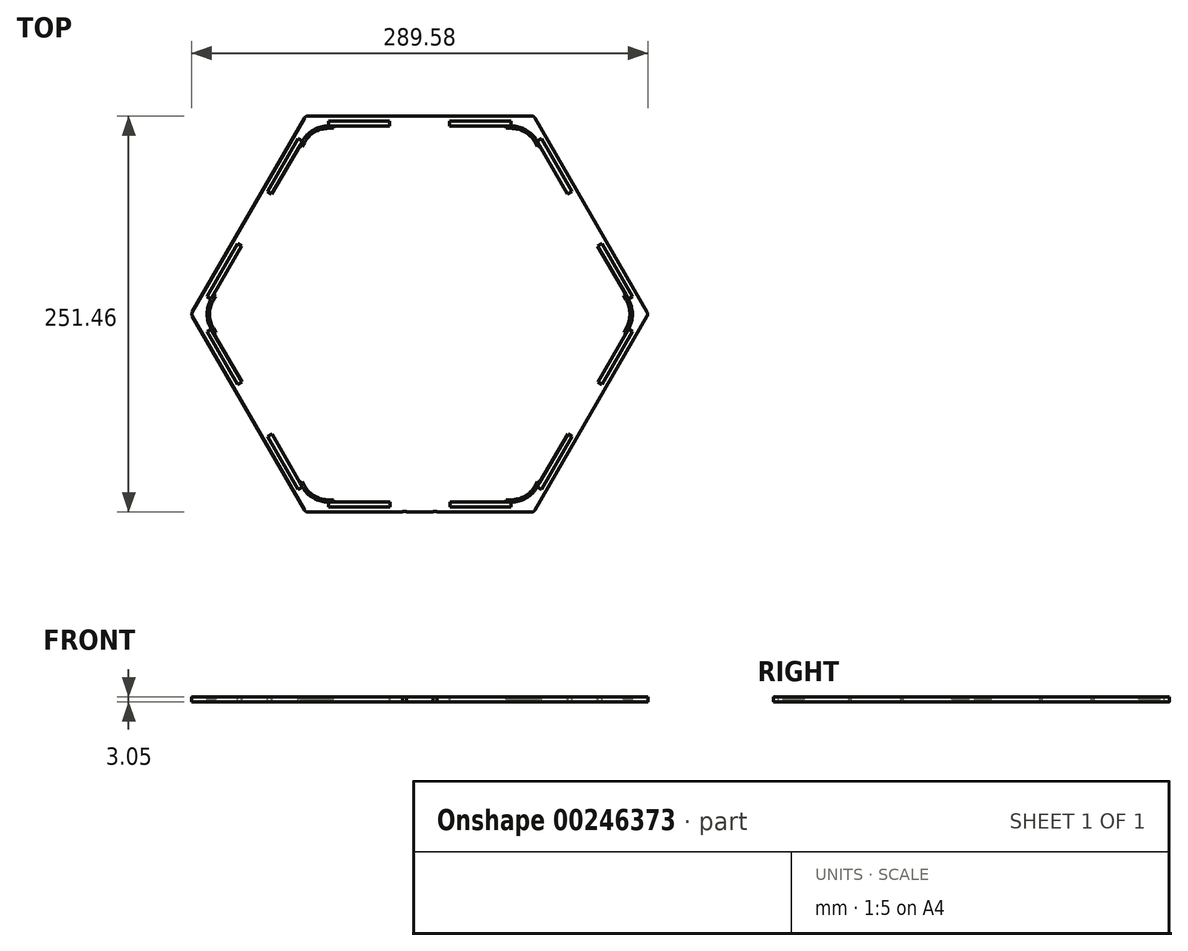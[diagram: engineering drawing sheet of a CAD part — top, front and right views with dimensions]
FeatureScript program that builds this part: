
annotation { "Feature Type Name" : "Feature", "Feature Type Description" : "" }
export const myFeature = defineFeature(function(context is Context, id is Id, definition is map)
    precondition{}
    {
        {
            var Q0;
            Q0=qCreatedBy(makeId("Top.planeOp"),FACE);
            var sketch = newSketch(context, id + "F0", { "sketchPlane" : qUnion([Q0])});
            skCircle(sketch, "E0.cCircle", {"center": v(0, 0) * mm, "radius": 125.73 * mm, "construction": true});
            skLineSegment(sketch, "E0.0", {"start": v(-137.85, 12.7) * mm, "end": v(-79.92, 113.03) * mm});
            skLineSegment(sketch, "E0.1", {"start": v(-57.93, 125.73) * mm, "end": v(57.93, 125.73) * mm});
            skLineSegment(sketch, "E0.2", {"start": v(79.92, 113.03) * mm, "end": v(137.85, 12.7) * mm});
            skLineSegment(sketch, "E0.3", {"start": v(137.85, -12.7) * mm, "end": v(79.92, -113.03) * mm});
            skLineSegment(sketch, "E0.4", {"start": v(57.93, -125.73) * mm, "end": v(-57.93, -125.73) * mm});
            skLineSegment(sketch, "E0.5", {"start": v(-79.92, -113.03) * mm, "end": v(-137.85, -12.7) * mm});
            skPoint(sketch, "E0.0.midPoint", {"position": v(-108.89, 62.87) * mm});
            skPoint(sketch, "E1.visualSharp", {"position": v(-72.6, 125.73) * mm});
            skArc(sketch, "E1.filletArc", {"start": v(-57.93, 125.73) * mm, "mid": v(-70.63, 122.33) * mm, "end": v(-79.92, 113.03) * mm});
            skPoint(sketch, "E2.visualSharp", {"position": v(72.6, 125.73) * mm});
            skArc(sketch, "E2.filletArc", {"start": v(79.92, 113.03) * mm, "mid": v(70.63, 122.33) * mm, "end": v(57.93, 125.73) * mm});
            skPoint(sketch, "E3.visualSharp", {"position": v(145.18, 0) * mm});
            skArc(sketch, "E3.filletArc", {"start": v(137.85, -12.7) * mm, "mid": v(141.25, 0) * mm, "end": v(137.85, 12.7) * mm});
            skPoint(sketch, "E4.visualSharp", {"position": v(72.6, -125.73) * mm});
            skArc(sketch, "E4.filletArc", {"start": v(57.93, -125.73) * mm, "mid": v(70.63, -122.33) * mm, "end": v(79.92, -113.03) * mm});
            skPoint(sketch, "E5.visualSharp", {"position": v(-72.6, -125.73) * mm});
            skArc(sketch, "E5.filletArc", {"start": v(-79.92, -113.03) * mm, "mid": v(-70.63, -122.33) * mm, "end": v(-57.93, -125.73) * mm});
            skPoint(sketch, "E6.visualSharp", {"position": v(-145.18, 0) * mm});
            skArc(sketch, "E6.filletArc", {"start": v(-137.85, 12.7) * mm, "mid": v(-141.25, 0) * mm, "end": v(-137.85, -12.7) * mm});
            skSolve(sketch);
        }
        {
            var Q0;
            Q0=qSketchRegion(id+"F0",true);
            extrude(context, id + "F1", {"entities" : qUnion([Q0]), "depth" : 3.05 * mm});
        }
        {
            var Q0;
            Q0=makeQuery(id+"F1.opExtrude","CAP_FACE",FACE,{"disambiguationData":[OSD([sQuery(id+"F0.wireOp",EDGE,"E0.0"),sQuery(id+"F0.wireOp",EDGE,"E0.1"),sQuery(id+"F0.wireOp",EDGE,"E0.2"),sQuery(id+"F0.wireOp",EDGE,"E0.3"),sQuery(id+"F0.wireOp",EDGE,"E0.4"),sQuery(id+"F0.wireOp",EDGE,"E0.5"),sQuery(id+"F0.wireOp",EDGE,"E1.filletArc"),sQuery(id+"F0.wireOp",EDGE,"E2.filletArc"),sQuery(id+"F0.wireOp",EDGE,"E3.filletArc"),sQuery(id+"F0.wireOp",EDGE,"E4.filletArc"),sQuery(id+"F0.wireOp",EDGE,"E5.filletArc"),sQuery(id+"F0.wireOp",EDGE,"E6.filletArc")])],"isStart":false});
            var sketch = newSketch(context, id + "F2", { "sketchPlane" : qUnion([Q0])});
            skLineSegment(sketch, "E7", {"start": v(-57.93, 122.56) * mm, "end": v(-57.93, 119.5) * mm});
            skLineSegment(sketch, "E8", {"start": v(-57.93, 119.5) * mm, "end": v(57.8, 119.5) * mm});
            skLineSegment(sketch, "E9", {"start": v(57.8, 119.5) * mm, "end": v(57.8, 122.56) * mm});
            skLineSegment(sketch, "E10.1.0", {"start": v(-135.1, 11.11) * mm, "end": v(-132.46, 9.59) * mm});
            skLineSegment(sketch, "E10.1.1", {"start": v(-132.46, 9.59) * mm, "end": v(-74.6, 109.82) * mm});
            skLineSegment(sketch, "E10.1.2", {"start": v(-74.6, 109.82) * mm, "end": v(-77.23, 111.34) * mm});
            skLineSegment(sketch, "E10.2.0", {"start": v(-77.17, -111.44) * mm, "end": v(-74.53, -109.92) * mm});
            skLineSegment(sketch, "E10.2.1", {"start": v(-74.53, -109.92) * mm, "end": v(-132.4, -9.7) * mm});
            skLineSegment(sketch, "E10.2.2", {"start": v(-132.4, -9.7) * mm, "end": v(-135.04, -11.22) * mm});
            skLineSegment(sketch, "E10.3.0", {"start": v(57.93, -122.55) * mm, "end": v(57.93, -119.5) * mm});
            skLineSegment(sketch, "E10.3.1", {"start": v(57.93, -119.5) * mm, "end": v(-57.8, -119.5) * mm});
            skLineSegment(sketch, "E10.3.2", {"start": v(-57.8, -119.5) * mm, "end": v(-57.8, -122.55) * mm});
            skLineSegment(sketch, "E10.4.0", {"start": v(135.1, -11.11) * mm, "end": v(132.46, -9.59) * mm});
            skLineSegment(sketch, "E10.4.1", {"start": v(132.46, -9.59) * mm, "end": v(74.6, -109.82) * mm});
            skLineSegment(sketch, "E10.4.2", {"start": v(74.6, -109.82) * mm, "end": v(77.23, -111.34) * mm});
            skLineSegment(sketch, "E10.5.0", {"start": v(77.17, 111.44) * mm, "end": v(74.53, 109.92) * mm});
            skLineSegment(sketch, "E10.5.1", {"start": v(74.53, 109.92) * mm, "end": v(132.4, 9.7) * mm});
            skLineSegment(sketch, "E10.5.2", {"start": v(132.4, 9.7) * mm, "end": v(135.04, 11.22) * mm});
            skPoint(sketch, "E10.center", {"position": v(0, 0) * mm});
            skLineSegment(sketch, "E11", {"start": v(-57.93, 122.56) * mm, "end": v(57.8, 122.56) * mm});
            skLineSegment(sketch, "E12.1.0", {"start": v(-135.1, 11.11) * mm, "end": v(-77.23, 111.34) * mm});
            skLineSegment(sketch, "E12.2.0", {"start": v(-77.17, -111.44) * mm, "end": v(-135.04, -11.22) * mm});
            skLineSegment(sketch, "E12.3.0", {"start": v(57.93, -122.56) * mm, "end": v(-57.8, -122.56) * mm});
            skLineSegment(sketch, "E12.4.0", {"start": v(135.1, -11.11) * mm, "end": v(77.23, -111.34) * mm});
            skLineSegment(sketch, "E12.5.0", {"start": v(77.17, 111.44) * mm, "end": v(135.04, 11.22) * mm});
            skSolve(sketch);
        }
        {
            var Q0;
            Q0=makeQuery(id+"F2.imprint","IMPRINT",FACE,{"disambiguationData":[TD([[makeQuery(id+"F2.imprint","IMPRINT",EDGE,{"derivedFrom":sQuery(id+"F2.wireOp",EDGE,"E10.2.0")}),1.0]])]});
            var Q1;
            Q1=makeQuery(id+"F2.imprint","IMPRINT",FACE,{"disambiguationData":[TD([[makeQuery(id+"F2.imprint","IMPRINT",EDGE,{"derivedFrom":sQuery(id+"F2.wireOp",EDGE,"E10.1.0")}),1.0]])]});
            var Q2;
            Q2=makeQuery(id+"F2.imprint","IMPRINT",FACE,{"disambiguationData":[TD([[makeQuery(id+"F2.imprint","IMPRINT",EDGE,{"derivedFrom":sQuery(id+"F2.wireOp",EDGE,"E7")}),1.0]])]});
            var Q3;
            Q3=makeQuery(id+"F2.imprint","IMPRINT",FACE,{"disambiguationData":[TD([[makeQuery(id+"F2.imprint","IMPRINT",EDGE,{"derivedFrom":sQuery(id+"F2.wireOp",EDGE,"E10.5.0")}),1.0]])]});
            var Q4;
            Q4=makeQuery(id+"F2.imprint","IMPRINT",FACE,{"disambiguationData":[TD([[makeQuery(id+"F2.imprint","IMPRINT",EDGE,{"derivedFrom":sQuery(id+"F2.wireOp",EDGE,"E10.4.0")}),1.0]])]});
            var Q5;
            Q5=makeQuery(id+"F2.imprint","IMPRINT",FACE,{"disambiguationData":[TD([[makeQuery(id+"F2.imprint","IMPRINT",EDGE,{"derivedFrom":sQuery(id+"F2.wireOp",EDGE,"E10.3.0")}),1.0]])]});
            extrude(context, id + "F3", {"entities" : qUnion([Q0, Q1, Q2, Q3, Q4, Q5]), "operationType" : NewBodyOperationType.REMOVE, "endBound" : BoundingType.THROUGH_ALL, "oppositeDirection" : true, "depth" : 25.4 * mm});
        }
        {
            var Q0;
            Q0=makeQuery(id+"F2.imprint","IMPRINT",FACE,{"disambiguationData":[TD([[makeQuery(id+"F2.imprint","IMPRINT",EDGE,{"derivedFrom":sQuery(id+"F2.wireOp",EDGE,"E7")}),-1.0]])]});
            var sketch = newSketch(context, id + "F4", { "sketchPlane" : qUnion([Q0])});
            skCircle(sketch, "E13", {"center": v(-62.3, 107.85) * mm, "radius": 7.89 * mm});
            skArc(sketch, "E14", {"start": v(-57.93, 119.5) * mm, "mid": v(-67.57, 116.9) * mm, "end": v(-74.6, 109.82) * mm, "construction": true});
            skLineSegment(sketch, "E15", {"start": v(-67.57, 116.9) * mm, "end": v(-62.3, 107.85) * mm, "construction": true});
            skPoint(sketch, "E16", {"position": v(-66.26, 114.67) * mm});
            skCircle(sketch, "E17.1.0", {"center": v(-124.55, -0.03) * mm, "radius": 7.89 * mm});
            skCircle(sketch, "E17.2.0", {"center": v(-62.25, -107.88) * mm, "radius": 7.89 * mm});
            skCircle(sketch, "E17.3.0", {"center": v(62.3, -107.85) * mm, "radius": 7.89 * mm});
            skCircle(sketch, "E17.4.0", {"center": v(124.55, 0.03) * mm, "radius": 7.89 * mm});
            skCircle(sketch, "E17.5.0", {"center": v(62.25, 107.88) * mm, "radius": 7.89 * mm});
            skPoint(sketch, "E17.center", {"position": v(0, 0) * mm});
            skSolve(sketch);
        }
        {
            var Q0;
            Q0=makeQuery(id+"F1.opExtrude","CAP_FACE",FACE,{"disambiguationData":[OSD([sQuery(id+"F0.wireOp",EDGE,"E0.0"),sQuery(id+"F0.wireOp",EDGE,"E0.1"),sQuery(id+"F0.wireOp",EDGE,"E0.2"),sQuery(id+"F0.wireOp",EDGE,"E0.3"),sQuery(id+"F0.wireOp",EDGE,"E0.4"),sQuery(id+"F0.wireOp",EDGE,"E0.5"),sQuery(id+"F0.wireOp",EDGE,"E1.filletArc"),sQuery(id+"F0.wireOp",EDGE,"E2.filletArc"),sQuery(id+"F0.wireOp",EDGE,"E3.filletArc"),sQuery(id+"F0.wireOp",EDGE,"E4.filletArc"),sQuery(id+"F0.wireOp",EDGE,"E5.filletArc"),sQuery(id+"F0.wireOp",EDGE,"E6.filletArc")])],"isStart":false});
            var sketch = newSketch(context, id + "F5", { "sketchPlane" : qUnion([Q0])});
            skPoint(sketch, "E18", {"position": v(0, -122.56) * mm});
            skPoint(sketch, "E19", {"position": v(9.58, -122.56) * mm});
            skPoint(sketch, "E20", {"position": v(-9.53, -122.56) * mm});
            skLineSegment(sketch, "E21.bottom", {"start": v(-10.8, -125.73) * mm, "end": v(-8.26, -125.73) * mm});
            skLineSegment(sketch, "E21.top", {"start": v(-10.8, -125.48) * mm, "end": v(-8.25, -125.48) * mm});
            skLineSegment(sketch, "E21.left", {"start": v(-10.8, -125.73) * mm, "end": v(-10.8, -125.48) * mm});
            skLineSegment(sketch, "E21.right", {"start": v(-8.25, -125.73) * mm, "end": v(-8.25, -125.48) * mm});
            skLineSegment(sketch, "E22.bottom", {"start": v(8.31, -125.73) * mm, "end": v(10.85, -125.73) * mm});
            skLineSegment(sketch, "E22.top", {"start": v(8.31, -125.48) * mm, "end": v(10.85, -125.48) * mm});
            skLineSegment(sketch, "E22.left", {"start": v(8.31, -125.73) * mm, "end": v(8.31, -125.48) * mm});
            skLineSegment(sketch, "E22.right", {"start": v(10.85, -125.73) * mm, "end": v(10.85, -125.48) * mm});
            skPoint(sketch, "E23", {"position": v(-9.53, -125.48) * mm});
            skPoint(sketch, "E24", {"position": v(9.58, -125.48) * mm});
            skSolve(sketch);
        }
        {
            var Q0;
            Q0=qSketchRegion(id+"F5",true);
            extrude(context, id + "F6", {"entities" : qUnion([Q0]), "operationType" : NewBodyOperationType.REMOVE, "endBound" : BoundingType.THROUGH_ALL, "oppositeDirection" : true, "depth" : 25.4 * mm});
        }
        {
            var Q0;
            Q0=makeQuery(id+"F1.opExtrude","CAP_FACE",FACE,{"disambiguationData":[OSD([sQuery(id+"F0.wireOp",EDGE,"E0.0"),sQuery(id+"F0.wireOp",EDGE,"E0.1"),sQuery(id+"F0.wireOp",EDGE,"E0.2"),sQuery(id+"F0.wireOp",EDGE,"E0.3"),sQuery(id+"F0.wireOp",EDGE,"E0.4"),sQuery(id+"F0.wireOp",EDGE,"E0.5"),sQuery(id+"F0.wireOp",EDGE,"E1.filletArc"),sQuery(id+"F0.wireOp",EDGE,"E2.filletArc"),sQuery(id+"F0.wireOp",EDGE,"E3.filletArc"),sQuery(id+"F0.wireOp",EDGE,"E4.filletArc"),sQuery(id+"F0.wireOp",EDGE,"E5.filletArc"),sQuery(id+"F0.wireOp",EDGE,"E6.filletArc")])],"isStart":false});
            var sketch = newSketch(context, id + "F7", { "sketchPlane" : qUnion([Q0])});
            skLineSegment(sketch, "E25", {"start": v(-79.92, 113.03) * mm, "end": v(-73.32, 124.46) * mm});
            skLineSegment(sketch, "E26", {"start": v(-71.12, 125.73) * mm, "end": v(-57.93, 125.73) * mm});
            skPoint(sketch, "E27.visualSharp", {"position": v(-72.6, 125.73) * mm});
            skArc(sketch, "E27.filletArc", {"start": v(-71.12, 125.73) * mm, "mid": v(-72.4, 125.39) * mm, "end": v(-73.32, 124.46) * mm});
            skLineSegment(sketch, "E28", {"start": v(-79.92, 113.03) * mm, "end": v(-57.93, 125.73) * mm});
            skLineSegment(sketch, "E29", {"start": v(57.93, 125.73) * mm, "end": v(71.12, 125.73) * mm});
            skLineSegment(sketch, "E30", {"start": v(73.32, 124.46) * mm, "end": v(79.92, 113.03) * mm});
            skLineSegment(sketch, "E31", {"start": v(-137.85, -12.7) * mm, "end": v(-144.45, -1.27) * mm});
            skLineSegment(sketch, "E32", {"start": v(-144.45, 1.27) * mm, "end": v(-137.85, 12.7) * mm});
            skLineSegment(sketch, "E33", {"start": v(57.93, -125.73) * mm, "end": v(71.12, -125.73) * mm});
            skLineSegment(sketch, "E34", {"start": v(73.32, -124.46) * mm, "end": v(79.92, -113.03) * mm});
            skLineSegment(sketch, "E35", {"start": v(137.85, 12.7) * mm, "end": v(144.45, 1.27) * mm});
            skLineSegment(sketch, "E36", {"start": v(144.45, -1.27) * mm, "end": v(137.85, -12.7) * mm});
            skPoint(sketch, "E37.visualSharp", {"position": v(72.6, 125.73) * mm});
            skArc(sketch, "E37.filletArc", {"start": v(73.32, 124.46) * mm, "mid": v(72.4, 125.39) * mm, "end": v(71.12, 125.73) * mm});
            skPoint(sketch, "E38.visualSharp", {"position": v(145.18, 0) * mm});
            skArc(sketch, "E38.filletArc", {"start": v(144.45, -1.27) * mm, "mid": v(144.79, 0) * mm, "end": v(144.45, 1.27) * mm});
            skPoint(sketch, "E39.visualSharp", {"position": v(72.6, -125.73) * mm});
            skArc(sketch, "E39.filletArc", {"start": v(71.12, -125.73) * mm, "mid": v(72.4, -125.39) * mm, "end": v(73.32, -124.46) * mm});
            skLineSegment(sketch, "E40", {"start": v(-79.92, -113.03) * mm, "end": v(-73.32, -124.46) * mm});
            skLineSegment(sketch, "E41", {"start": v(-71.12, -125.73) * mm, "end": v(-57.93, -125.73) * mm});
            skPoint(sketch, "E42.visualSharp", {"position": v(-72.6, -125.73) * mm});
            skArc(sketch, "E42.filletArc", {"start": v(-73.32, -124.46) * mm, "mid": v(-72.4, -125.39) * mm, "end": v(-71.12, -125.73) * mm});
            skPoint(sketch, "E43.visualSharp", {"position": v(-145.18, 0) * mm});
            skArc(sketch, "E43.filletArc", {"start": v(-144.45, 1.27) * mm, "mid": v(-144.79, 0) * mm, "end": v(-144.45, -1.27) * mm});
            skSolve(sketch);
        }
        {
            var Q0;
            Q0=qSketchRegion(id+"F7",true);
            var Q1;
            Q1=makeQuery(id+"F7.imprint","IMPRINT",FACE,{"disambiguationData":[TD([[makeQuery(id+"F7.imprint","IMPRINT",EDGE,{"derivedFrom":sQuery(id+"F7.wireOp",EDGE,"E31")}),-1.0]])]});
            var Q2;
            Q2=makeQuery(id+"F7.imprint","IMPRINT",FACE,{"disambiguationData":[TD([[makeQuery(id+"F7.imprint","IMPRINT",EDGE,{"derivedFrom":sQuery(id+"F7.wireOp",EDGE,"E40")}),1.0]])]});
            var Q3;
            Q3=makeQuery(id+"F7.imprint","IMPRINT",FACE,{"disambiguationData":[TD([[makeQuery(id+"F7.imprint","IMPRINT",EDGE,{"derivedFrom":sQuery(id+"F7.wireOp",EDGE,"E33")}),1.0]])]});
            var Q4;
            Q4=makeQuery(id+"F7.imprint","IMPRINT",FACE,{"disambiguationData":[TD([[makeQuery(id+"F7.imprint","IMPRINT",EDGE,{"derivedFrom":sQuery(id+"F7.wireOp",EDGE,"E35")}),-1.0]])]});
            var Q5;
            Q5=makeQuery(id+"F7.imprint","IMPRINT",FACE,{"disambiguationData":[TD([[makeQuery(id+"F7.imprint","IMPRINT",EDGE,{"derivedFrom":sQuery(id+"F7.wireOp",EDGE,"E29")}),-1.0]])]});
            extrude(context, id + "F8", {"entities" : qUnion([Q0, Q1, Q2, Q3, Q4, Q5]), "operationType" : NewBodyOperationType.ADD, "oppositeDirection" : true, "depth" : 3.05 * mm});
        }
        {
            var Q0;
            {var subQ0=sQuery(id+"F0.wireOp",EDGE,"E5.filletArc");var subQ1=sQuery(id+"F0.wireOp",EDGE,"E3.filletArc");var subQ2=sQuery(id+"F0.wireOp",EDGE,"E4.filletArc");var subQ3=sQuery(id+"F0.wireOp",EDGE,"E6.filletArc");var subQ4=sQuery(id+"F0.wireOp",EDGE,"E2.filletArc");Q0=makeQuery(id+"F8.boolean.opBoolean","MERGE",FACE,{"derivedFrom":[makeQuery(id+"F1.opExtrude","CAP_FACE",FACE,{"disambiguationData":[OSD([sQuery(id+"F0.wireOp",EDGE,"E0.0"),sQuery(id+"F0.wireOp",EDGE,"E0.1"),sQuery(id+"F0.wireOp",EDGE,"E0.2"),sQuery(id+"F0.wireOp",EDGE,"E0.3"),sQuery(id+"F0.wireOp",EDGE,"E0.4"),sQuery(id+"F0.wireOp",EDGE,"E0.5"),sQuery(id+"F0.wireOp",EDGE,"E1.filletArc"),subQ4,subQ1,subQ2,subQ0,subQ3])],"isStart":false}),makeQuery(id+"F8.opExtrude","CAP_FACE",FACE,{"disambiguationData":[OSD([sQuery(id+"F7.wireOp",EDGE,"E25"),sQuery(id+"F7.wireOp",EDGE,"E26"),sQuery(id+"F7.wireOp",EDGE,"E27.filletArc"),sQuery(id+"F7.wireOp",EDGE,"E28")])],"isStart":true}),makeQuery(id+"F8.opExtrude","CAP_FACE",FACE,{"disambiguationData":[OSD([subQ4,sQuery(id+"F7.wireOp",EDGE,"E29"),sQuery(id+"F7.wireOp",EDGE,"E30"),sQuery(id+"F7.wireOp",EDGE,"E37.filletArc")])],"isStart":true}),makeQuery(id+"F8.opExtrude","CAP_FACE",FACE,{"disambiguationData":[OSD([subQ3,sQuery(id+"F7.wireOp",EDGE,"E31"),sQuery(id+"F7.wireOp",EDGE,"E32"),sQuery(id+"F7.wireOp",EDGE,"E43.filletArc")])],"isStart":true}),makeQuery(id+"F8.opExtrude","CAP_FACE",FACE,{"disambiguationData":[OSD([subQ2,sQuery(id+"F7.wireOp",EDGE,"E33"),sQuery(id+"F7.wireOp",EDGE,"E34"),sQuery(id+"F7.wireOp",EDGE,"E39.filletArc")])],"isStart":true}),makeQuery(id+"F8.opExtrude","CAP_FACE",FACE,{"disambiguationData":[OSD([subQ1,sQuery(id+"F7.wireOp",EDGE,"E35"),sQuery(id+"F7.wireOp",EDGE,"E36"),sQuery(id+"F7.wireOp",EDGE,"E38.filletArc")])],"isStart":true}),makeQuery(id+"F8.opExtrude","CAP_FACE",FACE,{"disambiguationData":[OSD([subQ0,sQuery(id+"F7.wireOp",EDGE,"E40"),sQuery(id+"F7.wireOp",EDGE,"E41"),sQuery(id+"F7.wireOp",EDGE,"E42.filletArc")])],"isStart":true})]});}
            var sketch = newSketch(context, id + "F9", { "sketchPlane" : qUnion([Q0])});
            skArc(sketch, "E44", {"start": v(-57.93, 119.5) * mm, "mid": v(-67.57, 116.9) * mm, "end": v(-74.6, 109.82) * mm});
            skArc(sketch, "E45.0", {"start": v(-57.93, 117.98) * mm, "mid": v(-66.8, 115.6) * mm, "end": v(-73.27, 109.06) * mm});
            skLineSegment(sketch, "E46", {"start": v(-57.93, 117.98) * mm, "end": v(-57.93, 119.5) * mm});
            skLineSegment(sketch, "E47", {"start": v(-73.27, 109.06) * mm, "end": v(-74.6, 109.82) * mm});
            skArc(sketch, "E48", {"start": v(74.53, 109.92) * mm, "mid": v(67.45, 116.94) * mm, "end": v(57.8, 119.5) * mm});
            skArc(sketch, "E49", {"start": v(-132.46, 9.59) * mm, "mid": v(-135.03, -0.06) * mm, "end": v(-132.4, -9.7) * mm});
            skArc(sketch, "E50", {"start": v(-74.53, -109.92) * mm, "mid": v(-67.46, -116.97) * mm, "end": v(-57.8, -119.5) * mm});
            skArc(sketch, "E51", {"start": v(57.93, -119.5) * mm, "mid": v(67.55, -116.88) * mm, "end": v(74.6, -109.82) * mm});
            skArc(sketch, "E52", {"start": v(132.46, -9.59) * mm, "mid": v(135, 0.06) * mm, "end": v(132.4, 9.7) * mm});
            skArc(sketch, "E53.0", {"start": v(73.22, 109.15) * mm, "mid": v(66.69, 115.62) * mm, "end": v(57.8, 117.98) * mm});
            skArc(sketch, "E54.0", {"start": v(131.13, -8.83) * mm, "mid": v(133.47, 0.05) * mm, "end": v(131.08, 8.93) * mm});
            skArc(sketch, "E55.0", {"start": v(57.92, -117.98) * mm, "mid": v(66.78, -115.56) * mm, "end": v(73.27, -109.05) * mm});
            skArc(sketch, "E56.0", {"start": v(-73.21, -109.16) * mm, "mid": v(-66.7, -115.65) * mm, "end": v(-57.82, -117.98) * mm});
            skArc(sketch, "E57.0", {"start": v(-131.14, 8.83) * mm, "mid": v(-133.5, -0.05) * mm, "end": v(-131.08, -8.92) * mm});
            skLineSegment(sketch, "E58", {"start": v(-132.46, 9.59) * mm, "end": v(-131.14, 8.83) * mm});
            skLineSegment(sketch, "E59", {"start": v(-131.08, -8.92) * mm, "end": v(-132.4, -9.7) * mm});
            skLineSegment(sketch, "E60", {"start": v(-73.21, -109.16) * mm, "end": v(-74.53, -109.92) * mm});
            skLineSegment(sketch, "E61", {"start": v(-57.82, -117.98) * mm, "end": v(-57.8, -119.5) * mm});
            skLineSegment(sketch, "E62", {"start": v(57.92, -117.98) * mm, "end": v(57.93, -119.5) * mm});
            skLineSegment(sketch, "E63", {"start": v(131.13, -8.83) * mm, "end": v(132.46, -9.59) * mm});
            skLineSegment(sketch, "E64", {"start": v(131.08, 8.93) * mm, "end": v(132.4, 9.7) * mm});
            skLineSegment(sketch, "E65", {"start": v(73.27, -109.05) * mm, "end": v(74.6, -109.82) * mm});
            skLineSegment(sketch, "E66", {"start": v(57.8, 117.98) * mm, "end": v(57.8, 119.5) * mm});
            skLineSegment(sketch, "E67", {"start": v(73.22, 109.15) * mm, "end": v(74.53, 109.92) * mm});
            skLineSegment(sketch, "E68", {"start": v(-74.6, 109.82) * mm, "end": v(-76.18, 107.07) * mm});
            skLineSegment(sketch, "E69", {"start": v(-76.18, 107.07) * mm, "end": v(-74.84, 106.3) * mm});
            skLineSegment(sketch, "E70", {"start": v(-74.84, 106.3) * mm, "end": v(-73.27, 109.06) * mm});
            skLineSegment(sketch, "E71", {"start": v(-57.93, 119.5) * mm, "end": v(-54.75, 119.5) * mm});
            skLineSegment(sketch, "E72", {"start": v(-54.75, 119.5) * mm, "end": v(-54.75, 117.98) * mm});
            skLineSegment(sketch, "E73", {"start": v(-54.75, 117.98) * mm, "end": v(-57.93, 117.98) * mm});
            skLineSegment(sketch, "E74", {"start": v(-132.46, 9.59) * mm, "end": v(-130.87, 12.34) * mm});
            skLineSegment(sketch, "E75", {"start": v(-130.87, 12.34) * mm, "end": v(-129.56, 11.6) * mm});
            skLineSegment(sketch, "E76", {"start": v(-129.56, 11.6) * mm, "end": v(-131.14, 8.83) * mm});
            skLineSegment(sketch, "E77", {"start": v(-132.4, -9.7) * mm, "end": v(-130.81, -12.44) * mm});
            skLineSegment(sketch, "E78", {"start": v(-130.81, -12.44) * mm, "end": v(-129.5, -11.68) * mm});
            skLineSegment(sketch, "E79", {"start": v(-129.5, -11.68) * mm, "end": v(-131.08, -8.92) * mm});
            skLineSegment(sketch, "E80", {"start": v(-74.53, -109.92) * mm, "end": v(-76.12, -107.17) * mm});
            skLineSegment(sketch, "E81", {"start": v(-76.12, -107.17) * mm, "end": v(-74.8, -106.4) * mm});
            skLineSegment(sketch, "E82", {"start": v(-74.8, -106.4) * mm, "end": v(-73.21, -109.16) * mm});
            skLineSegment(sketch, "E83", {"start": v(-57.8, -119.5) * mm, "end": v(-54.63, -119.5) * mm});
            skLineSegment(sketch, "E84", {"start": v(-54.63, -119.5) * mm, "end": v(-54.63, -117.98) * mm});
            skLineSegment(sketch, "E85", {"start": v(-54.63, -117.98) * mm, "end": v(-57.82, -117.98) * mm});
            skLineSegment(sketch, "E86", {"start": v(57.93, -119.5) * mm, "end": v(54.75, -119.5) * mm});
            skLineSegment(sketch, "E87", {"start": v(54.75, -119.5) * mm, "end": v(54.75, -117.98) * mm});
            skLineSegment(sketch, "E88", {"start": v(54.75, -117.98) * mm, "end": v(57.92, -117.98) * mm});
            skLineSegment(sketch, "E89", {"start": v(74.6, -109.82) * mm, "end": v(76.18, -107.07) * mm});
            skLineSegment(sketch, "E90", {"start": v(76.18, -107.07) * mm, "end": v(74.86, -106.3) * mm});
            skLineSegment(sketch, "E91", {"start": v(74.86, -106.3) * mm, "end": v(73.27, -109.05) * mm});
            skLineSegment(sketch, "E92", {"start": v(132.46, -9.59) * mm, "end": v(130.87, -12.34) * mm});
            skLineSegment(sketch, "E93", {"start": v(130.87, -12.34) * mm, "end": v(129.55, -11.58) * mm});
            skLineSegment(sketch, "E94", {"start": v(129.55, -11.58) * mm, "end": v(131.13, -8.83) * mm});
            skLineSegment(sketch, "E95", {"start": v(132.4, 9.7) * mm, "end": v(130.81, 12.44) * mm});
            skLineSegment(sketch, "E96", {"start": v(130.81, 12.44) * mm, "end": v(129.5, 11.68) * mm});
            skLineSegment(sketch, "E97", {"start": v(129.5, 11.68) * mm, "end": v(131.08, 8.93) * mm});
            skLineSegment(sketch, "E98", {"start": v(74.53, 109.92) * mm, "end": v(76.12, 107.17) * mm});
            skLineSegment(sketch, "E99", {"start": v(76.12, 107.17) * mm, "end": v(74.8, 106.4) * mm});
            skLineSegment(sketch, "E100", {"start": v(74.8, 106.4) * mm, "end": v(73.22, 109.15) * mm});
            skLineSegment(sketch, "E101", {"start": v(57.8, 119.5) * mm, "end": v(54.63, 119.5) * mm});
            skLineSegment(sketch, "E102", {"start": v(54.63, 119.5) * mm, "end": v(54.63, 117.98) * mm});
            skLineSegment(sketch, "E103", {"start": v(54.63, 117.98) * mm, "end": v(57.8, 117.98) * mm});
            skSolve(sketch);
        }
        {
            var Q0;
            Q0=qSketchRegion(id+"F9",true);
            extrude(context, id + "F10", {"entities" : qUnion([Q0]), "operationType" : NewBodyOperationType.REMOVE, "oppositeDirection" : true, "depth" : 1.59 * mm});
        }
        {
            var Q0;
            {var subQ0=sQuery(id+"F0.wireOp",EDGE,"E5.filletArc");var subQ1=sQuery(id+"F0.wireOp",EDGE,"E3.filletArc");var subQ2=sQuery(id+"F0.wireOp",EDGE,"E4.filletArc");var subQ3=sQuery(id+"F0.wireOp",EDGE,"E6.filletArc");var subQ4=sQuery(id+"F0.wireOp",EDGE,"E2.filletArc");Q0=makeQuery(id+"F10.boolean.opBoolean","SPLIT",FACE,{"disambiguationData":[TD([makeQuery(id+"F3.boolean.opBoolean","COPY",FACE,{"derivedFrom":makeQuery(id+"F3.opExtrude","SWEPT_FACE",FACE,{"disambiguationData":[OSD([sQuery(id+"F2.wireOp",EDGE,"E8")])]})})])],"derivedFrom":makeQuery(id+"F8.boolean.opBoolean","MERGE",FACE,{"derivedFrom":[makeQuery(id+"F1.opExtrude","CAP_FACE",FACE,{"disambiguationData":[OSD([sQuery(id+"F0.wireOp",EDGE,"E0.0"),sQuery(id+"F0.wireOp",EDGE,"E0.1"),sQuery(id+"F0.wireOp",EDGE,"E0.2"),sQuery(id+"F0.wireOp",EDGE,"E0.3"),sQuery(id+"F0.wireOp",EDGE,"E0.4"),sQuery(id+"F0.wireOp",EDGE,"E0.5"),sQuery(id+"F0.wireOp",EDGE,"E1.filletArc"),subQ4,subQ1,subQ2,subQ0,subQ3])],"isStart":false}),makeQuery(id+"F8.opExtrude","CAP_FACE",FACE,{"disambiguationData":[OSD([sQuery(id+"F7.wireOp",EDGE,"E25"),sQuery(id+"F7.wireOp",EDGE,"E26"),sQuery(id+"F7.wireOp",EDGE,"E27.filletArc"),sQuery(id+"F7.wireOp",EDGE,"E28")])],"isStart":true}),makeQuery(id+"F8.opExtrude","CAP_FACE",FACE,{"disambiguationData":[OSD([subQ4,sQuery(id+"F7.wireOp",EDGE,"E29"),sQuery(id+"F7.wireOp",EDGE,"E30"),sQuery(id+"F7.wireOp",EDGE,"E37.filletArc")])],"isStart":true}),makeQuery(id+"F8.opExtrude","CAP_FACE",FACE,{"disambiguationData":[OSD([subQ3,sQuery(id+"F7.wireOp",EDGE,"E31"),sQuery(id+"F7.wireOp",EDGE,"E32"),sQuery(id+"F7.wireOp",EDGE,"E43.filletArc")])],"isStart":true}),makeQuery(id+"F8.opExtrude","CAP_FACE",FACE,{"disambiguationData":[OSD([subQ2,sQuery(id+"F7.wireOp",EDGE,"E33"),sQuery(id+"F7.wireOp",EDGE,"E34"),sQuery(id+"F7.wireOp",EDGE,"E39.filletArc")])],"isStart":true}),makeQuery(id+"F8.opExtrude","CAP_FACE",FACE,{"disambiguationData":[OSD([subQ1,sQuery(id+"F7.wireOp",EDGE,"E35"),sQuery(id+"F7.wireOp",EDGE,"E36"),sQuery(id+"F7.wireOp",EDGE,"E38.filletArc")])],"isStart":true}),makeQuery(id+"F8.opExtrude","CAP_FACE",FACE,{"disambiguationData":[OSD([subQ0,sQuery(id+"F7.wireOp",EDGE,"E40"),sQuery(id+"F7.wireOp",EDGE,"E41"),sQuery(id+"F7.wireOp",EDGE,"E42.filletArc")])],"isStart":true})]})});}
            var sketch = newSketch(context, id + "F11", { "sketchPlane" : qUnion([Q0])});
            skLineSegment(sketch, "E104.bottom", {"start": v(-19.1, 122.56) * mm, "end": v(19, 122.56) * mm});
            skLineSegment(sketch, "E104.top", {"start": v(-19.1, 119.5) * mm, "end": v(19, 119.5) * mm});
            skLineSegment(sketch, "E104.left", {"start": v(-19.1, 122.56) * mm, "end": v(-19.1, 119.5) * mm});
            skLineSegment(sketch, "E104.right", {"start": v(19, 122.56) * mm, "end": v(19, 119.5) * mm});
            skPoint(sketch, "E105", {"position": v(-0.06, 122.56) * mm});
            skLineSegment(sketch, "E106.1.0", {"start": v(-115.7, 44.73) * mm, "end": v(-96.64, 77.72) * mm});
            skPoint(sketch, "E106.1.1", {"position": v(-106.17, 61.23) * mm});
            skLineSegment(sketch, "E106.1.2", {"start": v(-113.05, 43.2) * mm, "end": v(-94, 76.2) * mm});
            skLineSegment(sketch, "E106.1.3", {"start": v(-115.7, 44.73) * mm, "end": v(-113.05, 43.2) * mm});
            skLineSegment(sketch, "E106.1.4", {"start": v(-96.64, 77.72) * mm, "end": v(-94, 76.2) * mm});
            skLineSegment(sketch, "E106.2.0", {"start": v(-96.58, -77.83) * mm, "end": v(-115.63, -44.83) * mm});
            skPoint(sketch, "E106.2.1", {"position": v(-106.1, -61.33) * mm});
            skLineSegment(sketch, "E106.2.2", {"start": v(-93.94, -76.3) * mm, "end": v(-113, -43.3) * mm});
            skLineSegment(sketch, "E106.2.3", {"start": v(-96.58, -77.83) * mm, "end": v(-93.94, -76.3) * mm});
            skLineSegment(sketch, "E106.2.4", {"start": v(-115.63, -44.83) * mm, "end": v(-113, -43.3) * mm});
            skLineSegment(sketch, "E106.3.0", {"start": v(19.1, -122.56) * mm, "end": v(-19, -122.56) * mm});
            skPoint(sketch, "E106.3.1", {"position": v(0.06, -122.56) * mm});
            skLineSegment(sketch, "E106.3.2", {"start": v(19.1, -119.5) * mm, "end": v(-19, -119.5) * mm});
            skLineSegment(sketch, "E106.3.3", {"start": v(19.1, -122.56) * mm, "end": v(19.1, -119.5) * mm});
            skLineSegment(sketch, "E106.3.4", {"start": v(-19, -122.56) * mm, "end": v(-19, -119.5) * mm});
            skLineSegment(sketch, "E106.4.0", {"start": v(115.7, -44.73) * mm, "end": v(96.64, -77.72) * mm});
            skPoint(sketch, "E106.4.1", {"position": v(106.17, -61.23) * mm});
            skLineSegment(sketch, "E106.4.2", {"start": v(113.05, -43.2) * mm, "end": v(94, -76.2) * mm});
            skLineSegment(sketch, "E106.4.3", {"start": v(115.7, -44.73) * mm, "end": v(113.05, -43.2) * mm});
            skLineSegment(sketch, "E106.4.4", {"start": v(96.64, -77.72) * mm, "end": v(94, -76.2) * mm});
            skLineSegment(sketch, "E106.5.0", {"start": v(96.58, 77.83) * mm, "end": v(115.63, 44.83) * mm});
            skPoint(sketch, "E106.5.1", {"position": v(106.1, 61.33) * mm});
            skLineSegment(sketch, "E106.5.2", {"start": v(93.94, 76.3) * mm, "end": v(113, 43.3) * mm});
            skLineSegment(sketch, "E106.5.3", {"start": v(96.58, 77.83) * mm, "end": v(93.94, 76.3) * mm});
            skLineSegment(sketch, "E106.5.4", {"start": v(115.63, 44.83) * mm, "end": v(113, 43.3) * mm});
            skPoint(sketch, "E106.center", {"position": v(0, 0) * mm});
            skSolve(sketch);
        }
        {
            var Q0;
            Q0 = qSketchRegion(id + "F11", true);
            var Q1;
            {var subQ0=sQuery(id+"F0.wireOp",EDGE,"E5.filletArc");var subQ1=sQuery(id+"F0.wireOp",EDGE,"E3.filletArc");var subQ2=sQuery(id+"F0.wireOp",EDGE,"E4.filletArc");var subQ3=sQuery(id+"F0.wireOp",EDGE,"E6.filletArc");var subQ4=sQuery(id+"F0.wireOp",EDGE,"E2.filletArc");Q1=makeQuery(id+"F8.boolean.opBoolean","MERGE",FACE,{"derivedFrom":[makeQuery(id+"F1.opExtrude","CAP_FACE",FACE,{"disambiguationData":[OSD([sQuery(id+"F0.wireOp",EDGE,"E0.0"),sQuery(id+"F0.wireOp",EDGE,"E0.1"),sQuery(id+"F0.wireOp",EDGE,"E0.2"),sQuery(id+"F0.wireOp",EDGE,"E0.3"),sQuery(id+"F0.wireOp",EDGE,"E0.4"),sQuery(id+"F0.wireOp",EDGE,"E0.5"),sQuery(id+"F0.wireOp",EDGE,"E1.filletArc"),subQ4,subQ1,subQ2,subQ0,subQ3])],"isStart":true}),makeQuery(id+"F8.opExtrude","CAP_FACE",FACE,{"disambiguationData":[OSD([sQuery(id+"F7.wireOp",EDGE,"E25"),sQuery(id+"F7.wireOp",EDGE,"E26"),sQuery(id+"F7.wireOp",EDGE,"E27.filletArc"),sQuery(id+"F7.wireOp",EDGE,"E28")])],"isStart":false}),makeQuery(id+"F8.opExtrude","CAP_FACE",FACE,{"disambiguationData":[OSD([subQ4,sQuery(id+"F7.wireOp",EDGE,"E29"),sQuery(id+"F7.wireOp",EDGE,"E30"),sQuery(id+"F7.wireOp",EDGE,"E37.filletArc")])],"isStart":false}),makeQuery(id+"F8.opExtrude","CAP_FACE",FACE,{"disambiguationData":[OSD([subQ3,sQuery(id+"F7.wireOp",EDGE,"E31"),sQuery(id+"F7.wireOp",EDGE,"E32"),sQuery(id+"F7.wireOp",EDGE,"E43.filletArc")])],"isStart":false}),makeQuery(id+"F8.opExtrude","CAP_FACE",FACE,{"disambiguationData":[OSD([subQ2,sQuery(id+"F7.wireOp",EDGE,"E33"),sQuery(id+"F7.wireOp",EDGE,"E34"),sQuery(id+"F7.wireOp",EDGE,"E39.filletArc")])],"isStart":false}),makeQuery(id+"F8.opExtrude","CAP_FACE",FACE,{"disambiguationData":[OSD([subQ1,sQuery(id+"F7.wireOp",EDGE,"E35"),sQuery(id+"F7.wireOp",EDGE,"E36"),sQuery(id+"F7.wireOp",EDGE,"E38.filletArc")])],"isStart":false}),makeQuery(id+"F8.opExtrude","CAP_FACE",FACE,{"disambiguationData":[OSD([subQ0,sQuery(id+"F7.wireOp",EDGE,"E40"),sQuery(id+"F7.wireOp",EDGE,"E41"),sQuery(id+"F7.wireOp",EDGE,"E42.filletArc")])],"isStart":false})]});}
            extrude(context, id + "F12", {"entities" : qUnion([Q0]), "operationType" : NewBodyOperationType.ADD, "endBound" : BoundingType.UP_TO_SURFACE, "oppositeDirection" : true, "endBoundEntityFace" : qUnion([Q1]), "depth" : 25.4 * mm});
        }
    });
